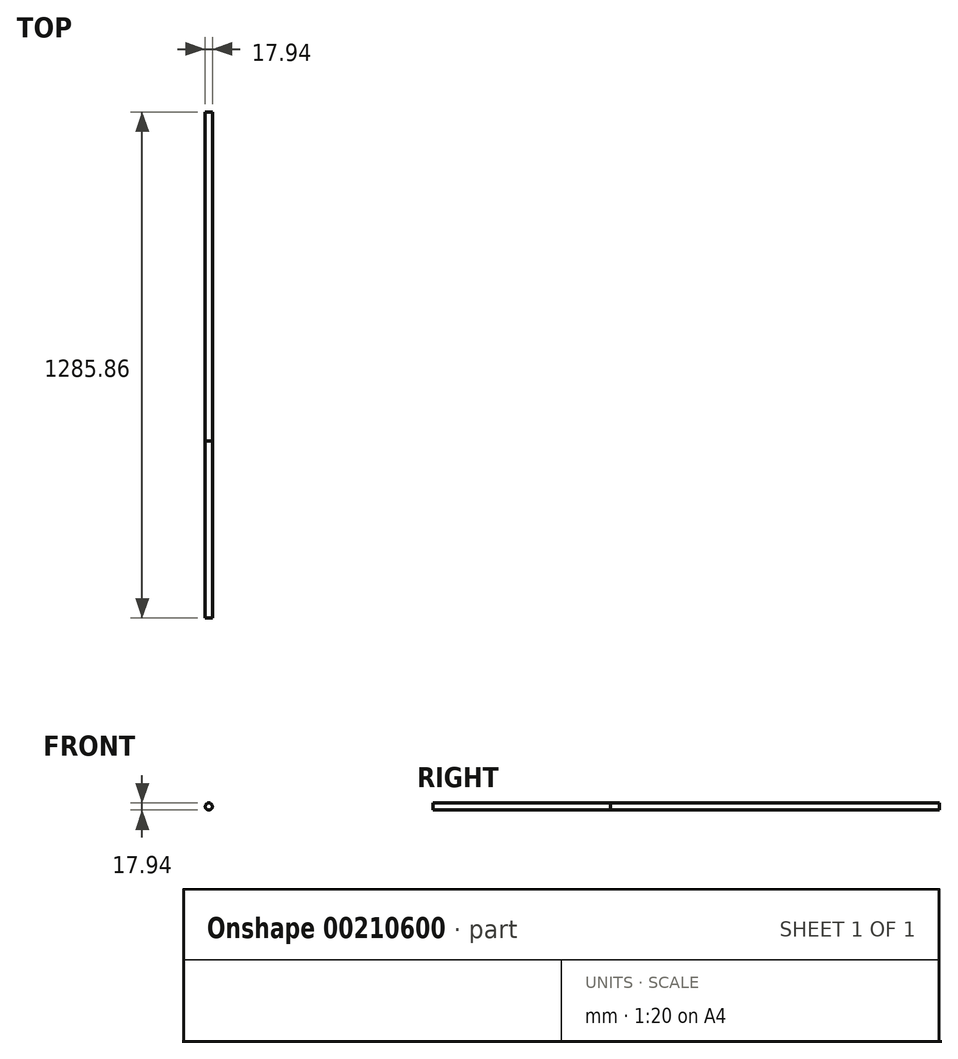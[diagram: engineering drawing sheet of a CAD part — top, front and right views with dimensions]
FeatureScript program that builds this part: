
annotation { "Feature Type Name" : "Feature", "Feature Type Description" : "" }
export const myFeature = defineFeature(function(context is Context, id is Id, definition is map)
    precondition{}
    {
        {
            assignVariable(context, id + "F0", {"name" : "rod_od", "anyValue" : 17.93 * mm});
        }
        {
            assignVariable(context, id + "F1", {"name" : "build_x", "anyValue" : 1250 * mm});
        }
        {
            assignVariable(context, id + "F2", {"name" : "build_y", "anyValue" : 800 * mm});
        }
        {
            assignVariable(context, id + "F3", {"name" : "width", "anyValue" : getVariable(context, 'build_x') + 2 * getVariable(context, 'rod_od')});
        }
        {
            assignVariable(context, id + "F4", {"name" : "depth", "anyValue" : getVariable(context, 'build_y') + 2 * getVariable(context, 'rod_od')});
        }
        {
            var Q0;
            Q0=qCreatedBy(makeId("Front.planeOp"),FACE);
            var sketch = newSketch(context, id + "F5", { "sketchPlane" : qUnion([Q0])});
            skCircle(sketch, "E0", {"center": v(0, 0) * mm, "radius": 8.96 * mm});
            skSolve(sketch);
        }
        {
            var Q0;
            Q0=qSketchRegion(id+"F5",true);
            extrude(context, id + "F6", {"entities" : qUnion([Q0]), "depth" : getVariable(context, 'depth')});
        }
        {
            var Q0;
            Q0=makeQuery(id+"F5.imprint","IMPRINT",FACE,{"disambiguationData":[TD([[makeQuery(id+"F5.imprint","IMPRINT",EDGE,{"derivedFrom":sQuery(id+"F5.wireOp",EDGE,"E0")}),1.0]])]});
            extrude(context, id + "F7", {"entities" : qUnion([Q0]), "depth" : getVariable(context, 'width')});
        }
    });
